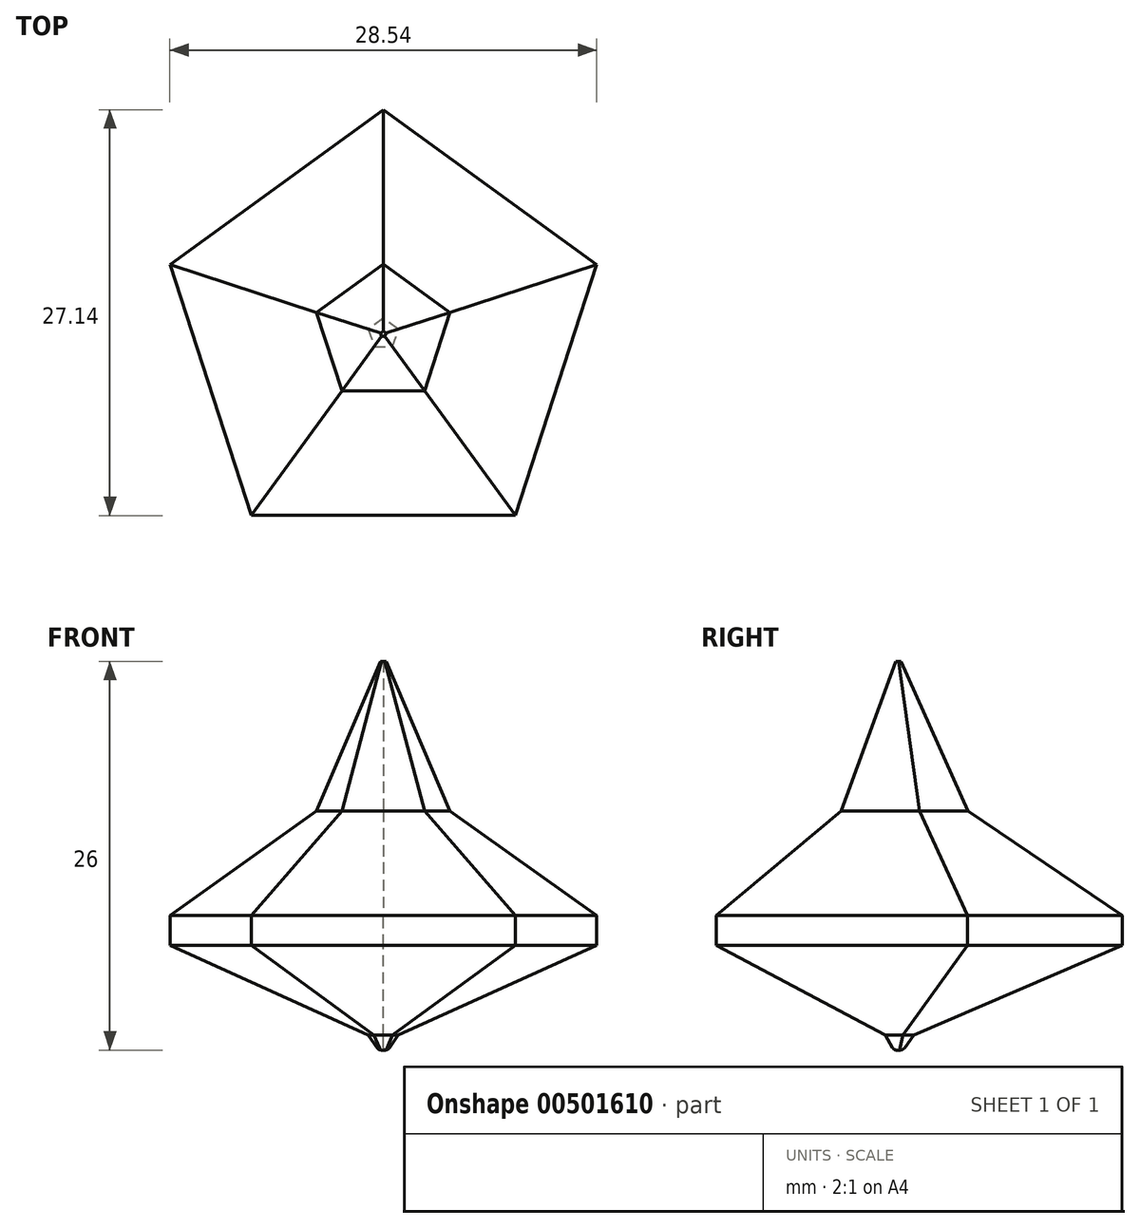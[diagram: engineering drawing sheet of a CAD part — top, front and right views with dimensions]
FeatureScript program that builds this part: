
annotation { "Feature Type Name" : "Feature", "Feature Type Description" : "" }
export const myFeature = defineFeature(function(context is Context, id is Id, definition is map)
    precondition{}
    {
        {
            var Q0;
            Q0=qCreatedBy(makeId("Top.planeOp"),FACE);
            var sketch = newSketch(context, id + "F0", { "sketchPlane" : qUnion([Q0])});
            skCircle(sketch, "E0.cCircle", {"center": v(0, 0) * mm, "radius": 15 * mm, "construction": true});
            skLineSegment(sketch, "E0.0", {"start": v(0, 15) * mm, "end": v(14.27, 4.64) * mm});
            skLineSegment(sketch, "E0.1", {"start": v(14.27, 4.64) * mm, "end": v(8.82, -12.14) * mm});
            skLineSegment(sketch, "E0.2", {"start": v(8.82, -12.14) * mm, "end": v(-8.82, -12.14) * mm});
            skLineSegment(sketch, "E0.3", {"start": v(-8.82, -12.14) * mm, "end": v(-14.27, 4.64) * mm});
            skLineSegment(sketch, "E0.4", {"start": v(-14.27, 4.64) * mm, "end": v(0, 15) * mm});
            skSolve(sketch);
        }
        {
            var Q0;
            Q0=makeQuery(id+"F0.imprint","IMPRINT",FACE,{"disambiguationData":[TD([[makeQuery(id+"F0.imprint","IMPRINT",EDGE,{"derivedFrom":sQuery(id+"F0.wireOp",EDGE,"E0.0")}),-1.0]])]});
            extrude(context, id + "F1", {"entities" : qUnion([Q0]), "depth" : 7 * mm, "hasDraft" : true, "draftAngle" : 50 * degree, "draftPullDirection" : true});
        }
        {
            var Q0;
            Q0=makeQuery(id+"F1.opExtrude","CAP_FACE",FACE,{"disambiguationData":[OSD([sQuery(id+"F0.wireOp",EDGE,"E0.0"),sQuery(id+"F0.wireOp",EDGE,"E0.1"),sQuery(id+"F0.wireOp",EDGE,"E0.2"),sQuery(id+"F0.wireOp",EDGE,"E0.3"),sQuery(id+"F0.wireOp",EDGE,"E0.4")])],"isStart":false});
            extrude(context, id + "F2", {"entities" : qUnion([Q0]), "operationType" : NewBodyOperationType.ADD, "depth" : 10 * mm, "hasDraft" : true, "draftAngle" : 20 * degree, "draftPullDirection" : true});
        }
        {
            var Q0;
            Q0=makeQuery(id+"F1.opExtrude","CAP_FACE",FACE,{"disambiguationData":[OSD([sQuery(id+"F0.wireOp",EDGE,"E0.0"),sQuery(id+"F0.wireOp",EDGE,"E0.1"),sQuery(id+"F0.wireOp",EDGE,"E0.2"),sQuery(id+"F0.wireOp",EDGE,"E0.3"),sQuery(id+"F0.wireOp",EDGE,"E0.4")])],"isStart":true});
            extrude(context, id + "F3", {"entities" : qUnion([Q0]), "operationType" : NewBodyOperationType.ADD, "depth" : 2 * mm});
        }
        {
            var Q0;
            Q0=makeQuery(id+"F3.opExtrude","CAP_FACE",FACE,{"disambiguationData":[OSD([sQuery(id+"F0.wireOp",EDGE,"E0.0"),sQuery(id+"F0.wireOp",EDGE,"E0.1"),sQuery(id+"F0.wireOp",EDGE,"E0.2"),sQuery(id+"F0.wireOp",EDGE,"E0.3"),sQuery(id+"F0.wireOp",EDGE,"E0.4")])],"isStart":false});
            extrude(context, id + "F4", {"entities" : qUnion([Q0]), "operationType" : NewBodyOperationType.ADD, "depth" : 6 * mm, "hasDraft" : true, "draftAngle" : 62 * degree, "draftPullDirection" : true});
        }
        {
            var Q0;
            Q0=makeQuery(id+"F4.opExtrude","CAP_FACE",FACE,{"disambiguationData":[OSD([sQuery(id+"F0.wireOp",EDGE,"E0.0"),sQuery(id+"F0.wireOp",EDGE,"E0.1"),sQuery(id+"F0.wireOp",EDGE,"E0.2"),sQuery(id+"F0.wireOp",EDGE,"E0.3"),sQuery(id+"F0.wireOp",EDGE,"E0.4")])],"isStart":false});
            extrude(context, id + "F5", {"entities" : qUnion([Q0]), "operationType" : NewBodyOperationType.ADD, "depth" : 1 * mm, "hasDraft" : true, "draftAngle" : 30 * degree, "draftPullDirection" : true});
        }
        {
            var Q0;
            Q0=makeQuery(id+"F5.opExtrude","CAP_FACE",FACE,{"disambiguationData":[OSD([sQuery(id+"F0.wireOp",EDGE,"E0.0"),sQuery(id+"F0.wireOp",EDGE,"E0.1"),sQuery(id+"F0.wireOp",EDGE,"E0.2"),sQuery(id+"F0.wireOp",EDGE,"E0.3"),sQuery(id+"F0.wireOp",EDGE,"E0.4")])],"isStart":false});
            fillet(context, id + "F6", {"entities" : qUnion([Q0]), "radius" : 0.3 * mm, "tangentPropagation" : true, "allowEdgeOverflow" : false});
        }
    });
